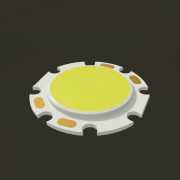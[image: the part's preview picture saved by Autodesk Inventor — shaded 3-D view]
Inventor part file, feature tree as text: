
AUTODESK INVENTOR PART (.ipt)
format: ipt  version: 2015 (Build 190159000, 159)  size: 317,952 bytes
history: native  units: mm
features: extrude x4, sketch x4, fillet x2, mirror x2
ambient origin geometry x8: Origin, YZ Plane, XZ Plane, XY Plane, X Axis, Y Axis, Z Axis, Center Point
bodies: Solid1 (feature_tree)
feature tree (12):
  extrude  "Extrusion1"  Depth=0.2mm
  fillet  "Fillet1"  Radius=20.0mm
  extrude  "Extrusion2"  Depth=1.2mm TaperAngle=0.0deg
  extrude  "Extrusion3"  Depth=0.43mm
  fillet  "Fillet2"  Radius=0.05mm
  extrude  "Extrusion4"  Depth=80.0mm TaperAngle=360.0deg
  mirror  "Mirror1"
  mirror  "Mirror2"
  sketch  "Sketch1"  dims[d6=1.0mm d7=0.0mm d8=0.2mm d9=20.0mm]
  sketch  "Sketch2"  dims[d10=0.513167mm d11=1.2mm d12=0.0mm]
  sketch  "Sketch3"  dims[d13=1.3mm d14=0.0mm d15=0.43mm d16=0.05mm d17=0.0mm]
  sketch  "Sketch4"  dims[d18=28.0mm d19=80.0mm d21=360.0deg d23=1.685mm d24=1.685mm d25=4.0mm d26=4.0mm]
